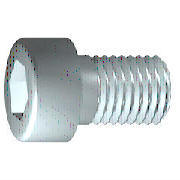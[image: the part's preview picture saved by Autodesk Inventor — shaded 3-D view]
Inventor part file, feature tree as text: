
AUTODESK INVENTOR PART (.ipt)
format: ipt  version: 2024.2 (Build 282272000, 272)  size: 200,192 bytes
history: native  units: mm (DEFAULTED — no unit token found)
features: extrude x1, plane x1, fillet x1
ambient origin geometry x7: Origin, YZ Plane, XY Plane, X Axis, Y Axis, Z Axis, Center Point
bodies: Solid1 (feature_tree), Body (feature_tree)
feature tree (3):
  extrude  "Slot"  Depth=6.875mm
  plane  "Work Plane1"
  fillet  "Fillet2"  Radius=0.276153mm
